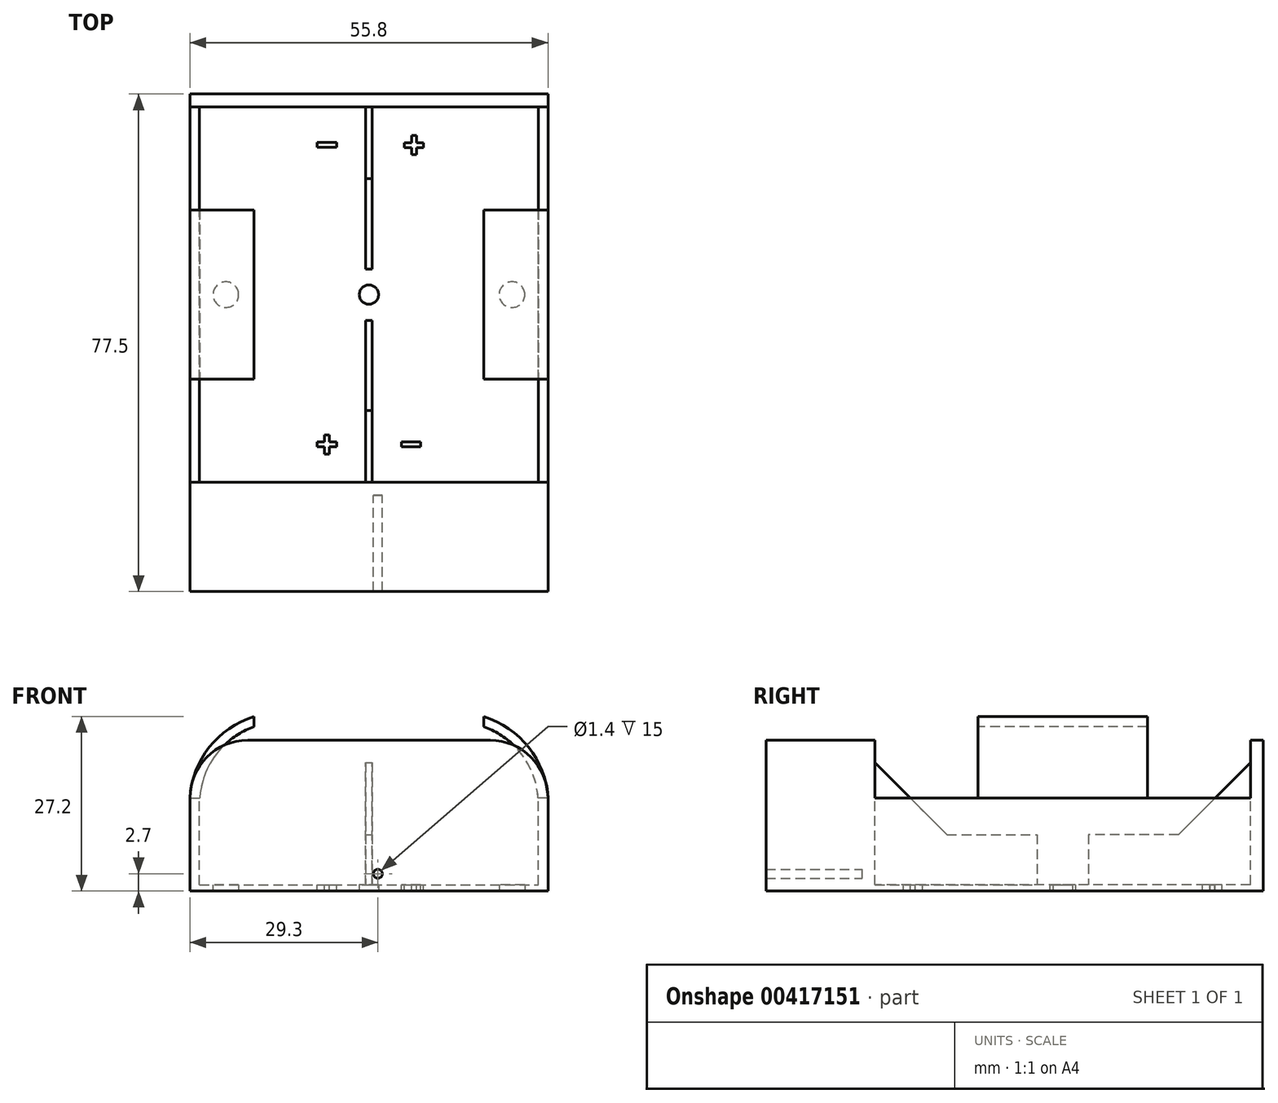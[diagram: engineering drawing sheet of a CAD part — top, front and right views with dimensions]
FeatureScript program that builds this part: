
annotation { "Feature Type Name" : "Feature", "Feature Type Description" : "" }
export const myFeature = defineFeature(function(context is Context, id is Id, definition is map)
    precondition{}
    {
        {
            var Q0;
            Q0=qCreatedBy(makeId("Top.planeOp"),FACE);
            var sketch = newSketch(context, id + "F0", { "sketchPlane" : qUnion([Q0])});
            skLineSegment(sketch, "E0.bottom", {"start": v(-27.9, 31.25) * mm, "end": v(27.9, 31.25) * mm});
            skLineSegment(sketch, "E0.top", {"start": v(-27.9, -31.25) * mm, "end": v(27.9, -31.25) * mm});
            skLineSegment(sketch, "E0.left", {"start": v(-27.9, 31.25) * mm, "end": v(-27.9, -31.25) * mm});
            skLineSegment(sketch, "E0.right", {"start": v(27.9, 31.25) * mm, "end": v(27.9, -31.25) * mm});
            skCircle(sketch, "E1", {"center": v(0, 0) * mm, "radius": 1.5 * mm});
            skCircle(sketch, "E2", {"center": v(-22.3, 0) * mm, "radius": 2 * mm});
            skCircle(sketch, "E3.MirrorC", {"center": v(22.3, 0) * mm, "radius": 2 * mm});
            skSolve(sketch);
        }
        {
            var Q0;
            Q0 = qSketchRegion(id + "F0", true);
            extrude(context, id + "F1", {"entities" : qUnion([Q0]), "depth" : 1 * mm});
        }
        {
            var Q0;
            Q0=makeQuery(id+"F1.opExtrude","SWEPT_FACE",FACE,{"disambiguationData":[OSD([sQuery(id+"F0.wireOp",EDGE,"E0.top")])]});
            var sketch = newSketch(context, id + "F2", { "sketchPlane" : qUnion([Q0])});
            skLineSegment(sketch, "E4.bottom", {"start": v(-27.9, 0) * mm, "end": v(27.9, 0) * mm});
            skLineSegment(sketch, "E4.top", {"start": v(-18.9, 23.5) * mm, "end": v(18.9, 23.5) * mm});
            skLineSegment(sketch, "E4.left", {"start": v(-27.9, 0) * mm, "end": v(-27.9, 14.5) * mm});
            skLineSegment(sketch, "E4.right", {"start": v(27.9, 0) * mm, "end": v(27.9, 14.5) * mm});
            skPoint(sketch, "E5.visualSharp", {"position": v(-27.9, 23.5) * mm});
            skArc(sketch, "E5.filletArc", {"start": v(-18.9, 23.5) * mm, "mid": v(-25.26, 20.86) * mm, "end": v(-27.9, 14.5) * mm});
            skCircle(sketch, "E6", {"center": v(-13.3, 14.1) * mm, "radius": 13.1 * mm, "construction": true});
            skPoint(sketch, "E7.visualSharp", {"position": v(27.9, 23.5) * mm});
            skArc(sketch, "E7.filletArc", {"start": v(27.9, 14.5) * mm, "mid": v(25.26, 20.86) * mm, "end": v(18.9, 23.5) * mm});
            skSolve(sketch);
        }
        {
            var Q0;
            Q0=makeQuery(id+"F2.imprint","IMPRINT",FACE,{"disambiguationData":[TD([[makeQuery(id+"F2.imprint","IMPRINT",EDGE,{"derivedFrom":sQuery(id+"F2.wireOp",EDGE,"E4.top")}),-1.0]])]});
            extrude(context, id + "F3", {"entities" : qUnion([Q0]), "oppositeDirection" : true, "depth" : 2 * mm});
        }
        {
            var Q0;
            Q0=makeQuery(id+"F3.opExtrude","SWEPT_BODY",BODY,{"disambiguationData":[OSD([sQuery(id+"F0.wireOp",EDGE,"E0.top"),sQuery(id+"F2.wireOp",EDGE,"E4.top"),sQuery(id+"F2.wireOp",EDGE,"E4.left"),sQuery(id+"F2.wireOp",EDGE,"E4.right"),sQuery(id+"F2.wireOp",EDGE,"E5.filletArc"),sQuery(id+"F2.wireOp",EDGE,"E7.filletArc")])]});
            var Q1;
            Q1=qCreatedBy(makeId("Front.planeOp"),FACE);
            mirror(context, id + "F4", {"operationType" : NewBodyOperationType.ADD, "entities" : qUnion([Q0]), "mirrorPlane" : qUnion([Q1])});
        }
        {
            var Q0;
            {var subQ0=makeQuery(id+"F3.opExtrude","SWEPT_FACE",FACE,{"disambiguationData":[OSD([sQuery(id+"F2.wireOp",EDGE,"E4.right")])]});Q0=makeQuery(id+"F4.boolean.opBoolean","MERGE",FACE,{"derivedFrom":[makeQuery(id+"F1.opExtrude","SWEPT_FACE",FACE,{"disambiguationData":[OSD([sQuery(id+"F0.wireOp",EDGE,"E0.right")])]}),subQ0,makeQuery(id+"F4.opPattern","COPY",FACE,{"derivedFrom":subQ0,"instanceName":"1"})]});}
            var sketch = newSketch(context, id + "F5", { "sketchPlane" : qUnion([Q0])});
            skLineSegment(sketch, "E8.bottom", {"start": v(-31.25, 0) * mm, "end": v(31.25, 0) * mm});
            skLineSegment(sketch, "E8.top", {"start": v(-31.25, 14.5) * mm, "end": v(31.25, 14.5) * mm});
            skLineSegment(sketch, "E8.left", {"start": v(-31.25, 0) * mm, "end": v(-31.25, 14.5) * mm});
            skLineSegment(sketch, "E8.right", {"start": v(31.25, 0) * mm, "end": v(31.25, 14.5) * mm});
            skSolve(sketch);
        }
        {
            var Q0;
            {var subQ1=makeQuery(id+"F3.opExtrude","CAP_EDGE",EDGE,{"disambiguationData":[OSD([sQuery(id+"F2.wireOp",EDGE,"E4.right")])],"isStart":false});Q0=makeQuery(id+"F5.imprint","IMPRINT",FACE,{"disambiguationData":[TD([[makeQuery(id+"F5.imprint","IMPRINT",EDGE,{"derivedFrom":subQ1}),-1.0]])]});}
            extrude(context, id + "F6", {"entities" : qUnion([Q0]), "operationType" : NewBodyOperationType.ADD, "oppositeDirection" : true, "depth" : 1.5 * mm});
        }
        {
            var Q0;
            Q0=makeQuery(id+"F1.opExtrude","SWEPT_BODY",BODY,{"disambiguationData":[OSD([sQuery(id+"F0.wireOp",EDGE,"E0.bottom"),sQuery(id+"F0.wireOp",EDGE,"E0.top"),sQuery(id+"F0.wireOp",EDGE,"E0.right"),sQuery(id+"F0.wireOp",EDGE,"E0.left"),sQuery(id+"F0.wireOp",EDGE,"E1")])]});
            var Q1;
            Q1=qCreatedBy(makeId("Right.planeOp"),FACE);
            mirror(context, id + "F7", {"operationType" : NewBodyOperationType.ADD, "entities" : qUnion([Q0]), "mirrorPlane" : qUnion([Q1])});
        }
        {
            var Q0;
            Q0=qCreatedBy(makeId("Right.planeOp"),FACE);
            cPlane(context, id + "F8", {"entities" : qUnion([Q0]), "cplaneType" : CPlaneType.OFFSET, "offset" : 0.5 * mm, "width" : 150 * mm, "height" : 150 * mm});
        }
        {
            var Q0;
            Q0=qCreatedBy(id+"F8.planeOp",FACE);
            var sketch = newSketch(context, id + "F9", { "sketchPlane" : qUnion([Q0])});
            skLineSegment(sketch, "E9", {"start": v(-29.25, 23.47) * mm, "end": v(-29.25, -1.32) * mm, "construction": true});
            skLineSegment(sketch, "E10", {"start": v(-42.4, 0) * mm, "end": v(14.5, 0) * mm, "construction": true});
            skLineSegment(sketch, "E11", {"start": v(-29.25, 20) * mm, "end": v(-18.05, 8.8) * mm});
            skLineSegment(sketch, "E12", {"start": v(-18.05, 8.8) * mm, "end": v(-4, 8.8) * mm});
            skLineSegment(sketch, "E13", {"start": v(-4, 8.8) * mm, "end": v(-4, 0) * mm});
            skLineSegment(sketch, "E14", {"start": v(-4, 0) * mm, "end": v(-29.25, 0) * mm});
            skLineSegment(sketch, "E15", {"start": v(-29.25, 0) * mm, "end": v(-29.25, 20) * mm});
            skSolve(sketch);
        }
        {
            var Q0;
            Q0=makeQuery(id+"F9.imprint","IMPRINT",FACE,{"disambiguationData":[TD([[makeQuery(id+"F9.imprint","IMPRINT",EDGE,{"derivedFrom":sQuery(id+"F9.wireOp",EDGE,"E11")}),-1.0]])]});
            extrude(context, id + "F10", {"entities" : qUnion([Q0]), "operationType" : NewBodyOperationType.ADD, "oppositeDirection" : true, "depth" : 1 * mm});
        }
        {
            var Q0;
            Q0=makeQuery(id+"F1.opExtrude","SWEPT_BODY",BODY,{"disambiguationData":[OSD([sQuery(id+"F0.wireOp",EDGE,"E0.bottom"),sQuery(id+"F0.wireOp",EDGE,"E0.top"),sQuery(id+"F0.wireOp",EDGE,"E0.right"),sQuery(id+"F0.wireOp",EDGE,"E0.left"),sQuery(id+"F0.wireOp",EDGE,"E1"),sQuery(id+"F0.wireOp",EDGE,"E2"),sQuery(id+"F0.wireOp",EDGE,"E3.MirrorC")])]});
            var Q1;
            Q1=qCreatedBy(makeId("Front.planeOp"),FACE);
            mirror(context, id + "F11", {"operationType" : NewBodyOperationType.ADD, "entities" : qUnion([Q0]), "mirrorPlane" : qUnion([Q1])});
        }
        {
            var Q0;
            Q0=qCreatedBy(makeId("Front.planeOp"),FACE);
            cPlane(context, id + "F12", {"entities" : qUnion([Q0]), "cplaneType" : CPlaneType.OFFSET, "offset" : 13.2 * mm, "width" : 150 * mm, "height" : 150 * mm});
        }
        {
            var Q0;
            Q0=qCreatedBy(id+"F12.planeOp",FACE);
            var sketch = newSketch(context, id + "F13", { "sketchPlane" : qUnion([Q0])});
            skLineSegment(sketch, "E16", {"start": v(-17.9, 27.2) * mm, "end": v(-17.9, 25.6) * mm});
            skLineSegment(sketch, "E17", {"start": v(-40.78, 1) * mm, "end": v(7.88, 1) * mm, "construction": true});
            skArc(sketch, "E18", {"start": v(-17.9, 25.6) * mm, "mid": v(-23.8, 21.32) * mm, "end": v(-26.37, 14.5) * mm});
            skLineSegment(sketch, "E19", {"start": v(-27.9, 0) * mm, "end": v(-27.9, 24.95) * mm, "construction": true});
            skLineSegment(sketch, "E20", {"start": v(-27.9, 14.5) * mm, "end": v(-26.37, 14.5) * mm});
            skArc(sketch, "E21", {"start": v(-17.9, 27.2) * mm, "mid": v(-24.89, 22.42) * mm, "end": v(-27.9, 14.5) * mm});
            skSolve(sketch);
        }
        {
            var Q0;
            Q0=makeQuery(id+"F13.imprint","IMPRINT",FACE,{"disambiguationData":[TD([[makeQuery(id+"F13.imprint","IMPRINT",EDGE,{"derivedFrom":sQuery(id+"F13.wireOp",EDGE,"E16")}),-1.0]])]});
            extrude(context, id + "F14", {"entities" : qUnion([Q0]), "operationType" : NewBodyOperationType.ADD, "oppositeDirection" : true, "depth" : 26.4 * mm});
        }
        {
            var Q0;
            Q0=makeQuery(id+"F1.opExtrude","SWEPT_BODY",BODY,{"disambiguationData":[OSD([sQuery(id+"F0.wireOp",EDGE,"E0.bottom"),sQuery(id+"F0.wireOp",EDGE,"E0.top"),sQuery(id+"F0.wireOp",EDGE,"E0.right"),sQuery(id+"F0.wireOp",EDGE,"E0.left"),sQuery(id+"F0.wireOp",EDGE,"E1"),sQuery(id+"F0.wireOp",EDGE,"E2"),sQuery(id+"F0.wireOp",EDGE,"E3.MirrorC")])]});
            var Q1;
            Q1=qCreatedBy(makeId("Right.planeOp"),FACE);
            mirror(context, id + "F15", {"operationType" : NewBodyOperationType.ADD, "entities" : qUnion([Q0]), "mirrorPlane" : qUnion([Q1])});
        }
        {
            var Q0;
            Q0=makeQuery(id+"F1.opExtrude","CAP_FACE",FACE,{"disambiguationData":[OSD([sQuery(id+"F0.wireOp",EDGE,"E0.bottom"),sQuery(id+"F0.wireOp",EDGE,"E0.top"),sQuery(id+"F0.wireOp",EDGE,"E0.right"),sQuery(id+"F0.wireOp",EDGE,"E0.left"),sQuery(id+"F0.wireOp",EDGE,"E1"),sQuery(id+"F0.wireOp",EDGE,"E2"),sQuery(id+"F0.wireOp",EDGE,"E3.MirrorC")])],"isStart":false});
            var sketch = newSketch(context, id + "F16", { "sketchPlane" : qUnion([Q0])});
            skLineSegment(sketch, "E22.bottom", {"start": v(-8.05, 23.73) * mm, "end": v(-5.05, 23.73) * mm});
            skLineSegment(sketch, "E22.top", {"start": v(-8.05, 22.98) * mm, "end": v(-5.05, 22.98) * mm});
            skLineSegment(sketch, "E22.left", {"start": v(-8.05, 23.73) * mm, "end": v(-8.05, 22.98) * mm});
            skLineSegment(sketch, "E22.right", {"start": v(-5.05, 23.73) * mm, "end": v(-5.05, 22.98) * mm});
            skLineSegment(sketch, "E23", {"start": v(-38.07, 0) * mm, "end": v(38.3, 0) * mm, "construction": true});
            skLineSegment(sketch, "E24", {"start": v(0, -35.94) * mm, "end": v(0, 44.47) * mm, "construction": true});
            skLineSegment(sketch, "E25.MirrorCS", {"start": v(-5.05, -23.73) * mm, "end": v(-5.05, -22.98) * mm});
            skLineSegment(sketch, "E26.MirrorCS", {"start": v(-8.05, -23.73) * mm, "end": v(-8.05, -22.98) * mm});
            skLineSegment(sketch, "E27.MirrorCS", {"start": v(-8.05, -22.98) * mm, "end": v(-6.92, -22.98) * mm});
            skLineSegment(sketch, "E28.MirrorCS", {"start": v(-8.05, -23.73) * mm, "end": v(-6.92, -23.73) * mm});
            skLineSegment(sketch, "E29.MirrorCS", {"start": v(5.05, -23.73) * mm, "end": v(5.05, -22.98) * mm});
            skLineSegment(sketch, "E30.MirrorCS", {"start": v(8.05, -23.73) * mm, "end": v(8.05, -22.98) * mm});
            skLineSegment(sketch, "E31.MirrorCS", {"start": v(8.05, -23.73) * mm, "end": v(5.05, -23.73) * mm});
            skLineSegment(sketch, "E32.MirrorCS", {"start": v(8.05, -22.98) * mm, "end": v(5.05, -22.98) * mm});
            skLineSegment(sketch, "E33", {"start": v(-6.55, -22.38) * mm, "end": v(-6.55, -24.83) * mm, "construction": true});
            skLineSegment(sketch, "E34", {"start": v(-8.3, -23.35) * mm, "end": v(-4.69, -23.35) * mm, "construction": true});
            skLineSegment(sketch, "E35.bottom", {"start": v(-6.92, -21.85) * mm, "end": v(-6.17, -21.85) * mm});
            skLineSegment(sketch, "E35.top", {"start": v(-6.92, -24.85) * mm, "end": v(-6.17, -24.85) * mm});
            skLineSegment(sketch, "E35.left", {"start": v(-6.92, -21.85) * mm, "end": v(-6.92, -22.98) * mm});
            skLineSegment(sketch, "E35.right", {"start": v(-6.17, -21.85) * mm, "end": v(-6.17, -22.98) * mm});
            skLineSegment(sketch, "E36.trimOffspring", {"start": v(-6.17, -22.98) * mm, "end": v(-5.05, -22.98) * mm});
            skLineSegment(sketch, "E37.trimOffspring", {"start": v(-6.17, -23.73) * mm, "end": v(-6.17, -24.85) * mm});
            skLineSegment(sketch, "E38.trimOffspring", {"start": v(-6.17, -23.73) * mm, "end": v(-5.05, -23.73) * mm});
            skLineSegment(sketch, "E39.trimOffspring", {"start": v(-6.92, -23.73) * mm, "end": v(-6.92, -24.85) * mm});
            skLineSegment(sketch, "E40.MirrorCS", {"start": v(8.52, 22.92) * mm, "end": v(8.52, 23.67) * mm});
            skLineSegment(sketch, "E41.MirrorCS", {"start": v(5.52, 22.92) * mm, "end": v(5.52, 23.67) * mm});
            skLineSegment(sketch, "E42.MirrorCS", {"start": v(5.52, 23.67) * mm, "end": v(6.65, 23.67) * mm});
            skLineSegment(sketch, "E43.MirrorCS", {"start": v(5.52, 22.92) * mm, "end": v(6.65, 22.92) * mm});
            skLineSegment(sketch, "E44", {"start": v(7.02, 24.27) * mm, "end": v(7.02, 21.82) * mm, "construction": true});
            skLineSegment(sketch, "E45", {"start": v(5.26, 23.3) * mm, "end": v(8.88, 23.3) * mm, "construction": true});
            skLineSegment(sketch, "E46.bottom", {"start": v(6.65, 24.8) * mm, "end": v(7.4, 24.8) * mm});
            skLineSegment(sketch, "E46.top", {"start": v(6.65, 21.8) * mm, "end": v(7.4, 21.8) * mm});
            skLineSegment(sketch, "E46.left", {"start": v(6.65, 24.8) * mm, "end": v(6.65, 23.67) * mm});
            skLineSegment(sketch, "E46.right", {"start": v(7.4, 24.8) * mm, "end": v(7.4, 23.67) * mm});
            skLineSegment(sketch, "E47.trimOffspring", {"start": v(7.4, 23.67) * mm, "end": v(8.52, 23.67) * mm});
            skLineSegment(sketch, "E48.trimOffspring", {"start": v(7.4, 22.92) * mm, "end": v(7.4, 21.8) * mm});
            skLineSegment(sketch, "E49.trimOffspring", {"start": v(7.4, 22.92) * mm, "end": v(8.52, 22.92) * mm});
            skLineSegment(sketch, "E50.trimOffspring", {"start": v(6.65, 22.92) * mm, "end": v(6.65, 21.8) * mm});
            skSolve(sketch);
        }
        {
            var Q0;
            Q0=makeQuery(id+"F16.imprint","IMPRINT",FACE,{"disambiguationData":[TD([[makeQuery(id+"F16.imprint","IMPRINT",EDGE,{"derivedFrom":sQuery(id+"F16.wireOp",EDGE,"E22.bottom")}),-1.0]])]});
            var Q1;
            Q1=makeQuery(id+"F16.imprint","IMPRINT",FACE,{"disambiguationData":[TD([[makeQuery(id+"F16.imprint","IMPRINT",EDGE,{"derivedFrom":sQuery(id+"F16.wireOp",EDGE,"E40.MirrorCS")}),1.0]])]});
            var Q2;
            Q2=makeQuery(id+"F16.imprint","IMPRINT",FACE,{"disambiguationData":[TD([[makeQuery(id+"F16.imprint","IMPRINT",EDGE,{"derivedFrom":sQuery(id+"F16.wireOp",EDGE,"E29.MirrorCS")}),-1.0]])]});
            var Q3;
            Q3=makeQuery(id+"F16.imprint","IMPRINT",FACE,{"disambiguationData":[TD([[makeQuery(id+"F16.imprint","IMPRINT",EDGE,{"derivedFrom":sQuery(id+"F16.wireOp",EDGE,"E25.MirrorCS")}),1.0]])]});
            extrude(context, id + "F17", {"entities" : qUnion([Q0, Q1, Q2, Q3]), "operationType" : NewBodyOperationType.REMOVE, "oppositeDirection" : true, "depth" : 1 * mm});
        }
        {
            var Q0;
            {var subQ0=sQuery(id+"F0.wireOp",EDGE,"E0.top");Q0=makeQuery(id+"F4.boolean.opBoolean","MERGE",FACE,{"derivedFrom":[makeQuery(id+"F1.opExtrude","SWEPT_FACE",FACE,{"disambiguationData":[OSD([subQ0])]}),makeQuery(id+"F3.opExtrude","CAP_FACE",FACE,{"disambiguationData":[OSD([subQ0,sQuery(id+"F2.wireOp",EDGE,"E4.top"),sQuery(id+"F2.wireOp",EDGE,"E4.left"),sQuery(id+"F2.wireOp",EDGE,"E4.right"),sQuery(id+"F2.wireOp",EDGE,"E5.filletArc"),sQuery(id+"F2.wireOp",EDGE,"E7.filletArc")])],"isStart":true})]});}
            var sketch = newSketch(context, id + "F18", { "sketchPlane" : qUnion([Q0])});
            skLineSegment(sketch, "E51", {"start": v(-33.83, 0) * mm, "end": v(26.67, 0) * mm, "construction": true});
            skLineSegment(sketch, "E52", {"start": v(-23, 2) * mm, "end": v(23, 2) * mm, "construction": true});
            skCircle(sketch, "E53", {"center": v(-1.4, 2.7) * mm, "radius": 0.7 * mm});
            skCircle(sketch, "E54.MirrorC", {"center": v(1.4, 2.7) * mm, "radius": 0.7 * mm});
            skSolve(sketch);
        }
        {
            var Q0;
            Q0=makeQuery(id+"F18.imprint","IMPRINT",FACE,{"disambiguationData":[TD([[makeQuery(id+"F18.imprint","IMPRINT",EDGE,{"derivedFrom":sQuery(id+"F18.wireOp",EDGE,"E53")}),1.0]])]});
            var Q1;
            Q1=makeQuery(id+"F18.imprint","IMPRINT",FACE,{"disambiguationData":[TD([[makeQuery(id+"F18.imprint","IMPRINT",EDGE,{"derivedFrom":sQuery(id+"F18.wireOp",EDGE,"E54.MirrorC")}),-1.0]])]});
            extrude(context, id + "F19", {"entities" : qUnion([Q0, Q1]), "operationType" : NewBodyOperationType.ADD, "depth" : 15 * mm});
        }
    });
